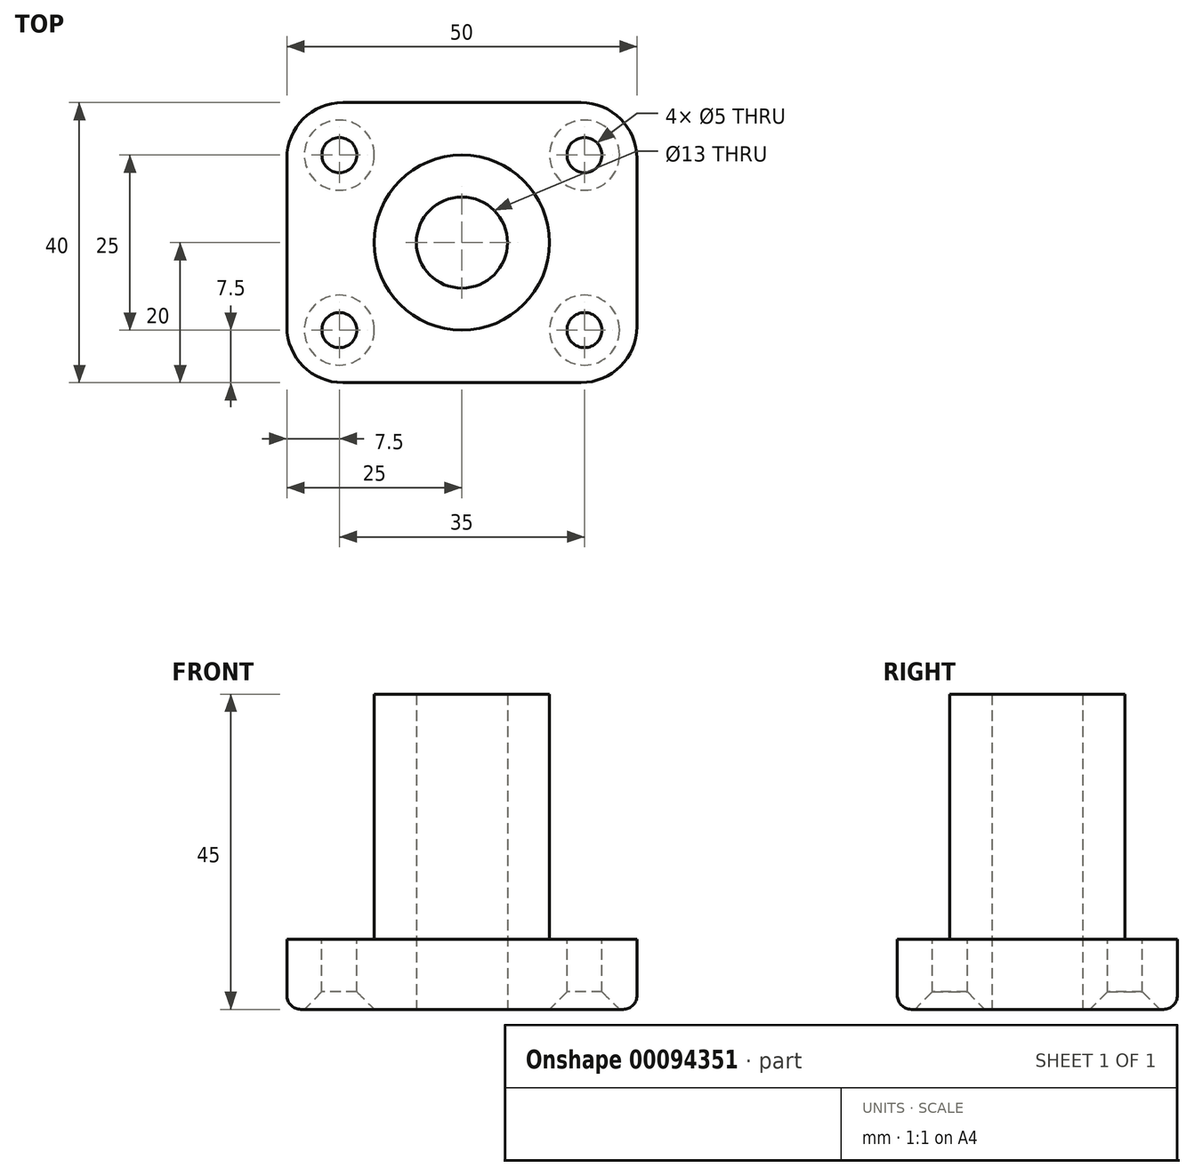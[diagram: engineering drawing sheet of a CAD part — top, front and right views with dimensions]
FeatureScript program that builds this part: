
annotation { "Feature Type Name" : "Feature", "Feature Type Description" : "" }
export const myFeature = defineFeature(function(context is Context, id is Id, definition is map)
    precondition{}
    {
        {
            var Q0;
            Q0=qCreatedBy(makeId("Top.planeOp"),FACE);
            var sketch = newSketch(context, id + "F0", { "sketchPlane" : qUnion([Q0])});
            skCircle(sketch, "E0", {"center": v(0, 0) * mm, "radius": 15 * mm});
            skSolve(sketch);
        }
        {
            var Q0;
            Q0=qCreatedBy(makeId("Top.planeOp"),FACE);
            var sketch = newSketch(context, id + "F1", { "sketchPlane" : qUnion([Q0])});
            skLineSegment(sketch, "E1.bottom", {"start": v(25, -20) * mm, "end": v(-25, -20) * mm});
            skLineSegment(sketch, "E1.top", {"start": v(25, 20) * mm, "end": v(-25, 20) * mm});
            skLineSegment(sketch, "E1.left", {"start": v(25, -20) * mm, "end": v(25, 20) * mm});
            skLineSegment(sketch, "E1.right", {"start": v(-25, -20) * mm, "end": v(-25, 20) * mm});
            skPoint(sketch, "E1.middle", {"position": v(0, 0) * mm});
            skSolve(sketch);
        }
        {
            var Q0;
            Q0=makeQuery(id+"F1.imprint","IMPRINT",FACE,{"disambiguationData":[TD([[makeQuery(id+"F1.imprint","IMPRINT",EDGE,{"derivedFrom":sQuery(id+"F1.wireOp",EDGE,"E1.bottom")}),-1.0]])]});
            var Q1;
            Q1=makeQuery(id+"F1.imprint","IMPRINT",FACE,{"disambiguationData":[TD([[makeQuery(id+"F1.imprint","IMPRINT",EDGE,{"derivedFrom":makeQuery(id+"FSAw8REgiUom5OK_0.opLoft","MID_CAP_EDGE",EDGE,{"disambiguationData":[OSD([sQuery(id+"F0.wireOp",EDGE,"E0")])],"capPos":0.0})}),-1.0]])]});
            extrude(context, id + "F2", {"entities" : qUnion([Q0, Q1]), "depth" : 10 * mm});
        }
        {
            var Q0;
            Q0=makeQuery(id+"F2.opExtrude","SWEPT_EDGE",EDGE,{"disambiguationData":[OSD([sQuery(id+"F1.wireOp",EDGE,"E1.top"),sQuery(id+"F1.wireOp",EDGE,"E1.right")])]});
            var Q1;
            Q1=makeQuery(id+"F2.opExtrude","SWEPT_EDGE",EDGE,{"disambiguationData":[OSD([sQuery(id+"F1.wireOp",EDGE,"E1.top"),sQuery(id+"F1.wireOp",EDGE,"E1.left")])]});
            var Q2;
            Q2=makeQuery(id+"F2.opExtrude","SWEPT_EDGE",EDGE,{"disambiguationData":[OSD([sQuery(id+"F1.wireOp",EDGE,"E1.bottom"),sQuery(id+"F1.wireOp",EDGE,"E1.left")])]});
            var Q3;
            Q3=makeQuery(id+"F2.opExtrude","SWEPT_EDGE",EDGE,{"disambiguationData":[OSD([sQuery(id+"F1.wireOp",EDGE,"E1.bottom"),sQuery(id+"F1.wireOp",EDGE,"E1.right")])]});
            fillet(context, id + "F3", {"entities" : qUnion([Q0, Q1, Q2, Q3]), "radius" : 8 * mm, "tangentPropagation" : true, "allowEdgeOverflow" : false});
        }
        {
            var Q0;
            Q0=makeQuery(id+"F2.opExtrude","CAP_FACE",FACE,{"disambiguationData":[OSD([sQuery(id+"F1.wireOp",EDGE,"E1.bottom"),sQuery(id+"F1.wireOp",EDGE,"E1.top"),sQuery(id+"F1.wireOp",EDGE,"E1.left"),sQuery(id+"F1.wireOp",EDGE,"E1.right")])],"isStart":false});
            var sketch = newSketch(context, id + "F4", { "sketchPlane" : qUnion([Q0])});
            skLineSegment(sketch, "E2.bottom", {"start": v(17.5, 12.5) * mm, "end": v(-17.5, 12.5) * mm});
            skLineSegment(sketch, "E2.top", {"start": v(17.5, -12.5) * mm, "end": v(-17.5, -12.5) * mm});
            skLineSegment(sketch, "E2.left", {"start": v(17.5, 12.5) * mm, "end": v(17.5, -12.5) * mm});
            skLineSegment(sketch, "E2.right", {"start": v(-17.5, 12.5) * mm, "end": v(-17.5, -12.5) * mm});
            skPoint(sketch, "E2.middle", {"position": v(0, 0) * mm});
            skSolve(sketch);
        }
        {
            var Q0;
            Q0=makeQuery(id+"F2.opExtrude","CAP_FACE",FACE,{"disambiguationData":[OSD([sQuery(id+"F1.wireOp",EDGE,"E1.bottom"),sQuery(id+"F1.wireOp",EDGE,"E1.top"),sQuery(id+"F1.wireOp",EDGE,"E1.left"),sQuery(id+"F1.wireOp",EDGE,"E1.right")])],"isStart":true});
            var sketch = newSketch(context, id + "F5", { "sketchPlane" : qUnion([Q0])});
            skPoint(sketch, "E3.0", {"position": v(-17.5, 12.5) * mm});
            skPoint(sketch, "E4.0", {"position": v(-17.5, -12.5) * mm});
            skPoint(sketch, "E5.0", {"position": v(17.5, -12.5) * mm});
            skPoint(sketch, "E6.0", {"position": v(17.5, 12.5) * mm});
            skSolve(sketch);
        }
        {
            var Q0;
            Q0=sQuery(id+"F5.wireOp",VERTEX,"E6.0");
            var Q1;
            Q1=sQuery(id+"F5.wireOp",VERTEX,"E3.0");
            var Q2;
            Q2=sQuery(id+"F5.wireOp",VERTEX,"E4.0");
            var Q3;
            Q3=sQuery(id+"F5.wireOp",VERTEX,"E5.0");
            var Q4;
            Q4=makeQuery(id+"F2.opExtrude","SWEPT_BODY",BODY,{"disambiguationData":[OSD([sQuery(id+"F1.wireOp",EDGE,"E1.bottom"),sQuery(id+"F1.wireOp",EDGE,"E1.top"),sQuery(id+"F1.wireOp",EDGE,"E1.left"),sQuery(id+"F1.wireOp",EDGE,"E1.right")])]});
            hole(context, id + "F6", {"style" : HoleStyle.C_SINK, "endStyle" : HoleEndStyle.BLIND, "holeDiameter" : 5 * mm, "cSinkDiameter" : 10 * mm, "cSinkAngle" : 90 * degree, "holeDepth" : 20 * mm, "tappedDepth" : 12 * mm, "tapClearance" : 3, "locations" : qUnion([Q0, Q1, Q2, Q3]), "scope" : qUnion([Q4]), "startStyle" : HoleStartStyle.SKETCH});
        }
        {
            var Q0;
            Q0=makeQuery(id+"F2.opExtrude","CAP_EDGE",EDGE,{"disambiguationData":[OSD([sQuery(id+"F1.wireOp",EDGE,"E1.bottom")])],"isStart":true});
            fillet(context, id + "F7", {"entities" : qUnion([Q0]), "radius" : 2 * mm, "tangentPropagation" : true, "allowEdgeOverflow" : false});
        }
        {
            var Q0;
            Q0=makeQuery(id+"F2.opExtrude","CAP_FACE",FACE,{"disambiguationData":[OSD([sQuery(id+"F1.wireOp",EDGE,"E1.bottom"),sQuery(id+"F1.wireOp",EDGE,"E1.top"),sQuery(id+"F1.wireOp",EDGE,"E1.left"),sQuery(id+"F1.wireOp",EDGE,"E1.right")])],"isStart":false});
            var sketch = newSketch(context, id + "F8", { "sketchPlane" : qUnion([Q0])});
            skCircle(sketch, "E7", {"center": v(0, 0) * mm, "radius": 12.5 * mm});
            skCircle(sketch, "E8", {"center": v(0, 0) * mm, "radius": 6.5 * mm});
            skSolve(sketch);
        }
        {
            var Q0;
            Q0=makeQuery(id+"F8.imprint","IMPRINT",FACE,{"disambiguationData":[TD([[makeQuery(id+"F8.imprint","IMPRINT",EDGE,{"derivedFrom":sQuery(id+"F8.wireOp",EDGE,"E7")}),1.0]])]});
            extrude(context, id + "F9", {"entities" : qUnion([Q0]), "operationType" : NewBodyOperationType.ADD, "depth" : 35 * mm});
        }
        {
            var Q0;
            Q0=makeQuery(id+"F9.boolean.opBoolean","SPLIT",FACE,{"disambiguationData":[TD([makeQuery(id+"F9.opExtrude","SWEPT_FACE",FACE,{"disambiguationData":[OSD([sQuery(id+"F8.wireOp",EDGE,"E8")])]})])],"derivedFrom":makeQuery(id+"F2.opExtrude","CAP_FACE",FACE,{"disambiguationData":[OSD([sQuery(id+"F1.wireOp",EDGE,"E1.bottom"),sQuery(id+"F1.wireOp",EDGE,"E1.top"),sQuery(id+"F1.wireOp",EDGE,"E1.left"),sQuery(id+"F1.wireOp",EDGE,"E1.right")])],"isStart":false})});
            extrude(context, id + "F10", {"entities" : qUnion([Q0]), "operationType" : NewBodyOperationType.REMOVE, "oppositeDirection" : true, "depth" : 25 * mm});
        }
    });
